# Revit family: Plumbing-Faucet-Sloan-Valve-SF-2250
name_source: partatom
category: Plumbing Fixtures
units: mm (PartAtom-declared; Revit-internal decimal feet)

## family parameters
Cut with Voids When Loaded = No
Host = Face
OmniClass Number = 23.45.55.14
OmniClass Title = Single Faucets
Part Type = Normal
Room Calculation Point = No
Round Connector Dimension = Use Diameter
Shared = No

## types (9) — shared parameters
Assembly Code = D2010
CW Connection = Yes
CWFU = 1.5
Cold Water Connection Diameter = 0"
Default Elevation = 0"
Depth = 6 5/8"
Edition number = 1
HW Connection = Yes
HWFU = 1.5
Height = 10"
Hot Water Connection Diameter = 0"
Keynote = 15410
Manufacturer = Sloan Valve
Product Material = Sloan Valve - Finish - Polished Chrome
Product data url = https://bimobject.com
URL = www.sloanvalve.com
Valve Pressure Drop = 0.00 psi
Vent Connection = No
Waste Connection = No
Width = 6 1/4"
z_Trim Plate Length = 6 1/4"
zero-valued in all types: WFU

## per-type parameters (varying)
| type | Description | Part Number | Water Flow |
| SF-2250-4-BAT-BDM-CP-0.35GPM-MLM-IR-FCT | 4" Trim Plate, Battery Power Supply, Below Deck Manual Mixing Valve, Polished Chrome Finish, 0.35 gpm, Multi-Laminar Spray, Infrared Sensor, Sloan® Battery-Powered Deck-Mounted Gooseneck Body Faucet. | 3362180 | 0 GPM |
| SF-2250-4-BAT-BDM-CP-1.0GPM-LAM-IR-FCT | 4" Trim Plate, Battery Power Supply, Below Deck Manual Mixing Valve, Polished Chrome Finish, 1.0 gpm, Laminar Spray, Infrared Sensor, Sloan® Battery-Powered Deck-Mounted Gooseneck Body Faucet. | 3362151 | 1 GPM |
| SF-2250-4-BAT-BDM-CP-1.5GPM-LAM-IR-FCT | 4" Trim Plate, Battery Power Supply, Below Deck Manual Mixing Valve, Polished Chrome Finish, 1.5 gpm, Laminar Spray, Infrared Sensor, Sloan® Battery-Powered Deck-Mounted Gooseneck Body Faucet. | 3362148 | 2 GPM |
| SF-2250-4-BAT-BDM-CP-2.2GPM-LAM-IR-FCT | 4" Trim Plate, Battery Power Supply, Below Deck Manual Mixing Valve, Polished Chrome Finish, 2.2 gpm, Laminar Spray, Infrared Sensor, Sloan® Battery-Powered Deck-Mounted Gooseneck Body Faucet. | 3362112 | 2 GPM |
| SF-2250-4-BAT-TEE-CP-0.35GPM-MLM-IR-FCT | 4" Trim Plate, Battery Power Supply, Back-Check Tee, Polished Chrome Finish, 0.35 gpm, Multi-Laminar Spray, Infrared Sensor, Sloan® Battery-Powered Deck-Mounted Gooseneck Body Faucet. | 3362173 | 0 GPM |
| SF-2250-4-BAT-TEE-CP-0.5GPM-MLM-IR-FCT | 4" Trim Plate, Battery Power Supply, Back-Check Tee, Polished Chrome Finish, 0.5 gpm, Multi-Laminar Spray, Infrared Sensor, Sloan® Battery-Powered Deck-Mounted Gooseneck Body Faucet. | 3362144 | 1 GPM |
| SF-2250-4-BAT-TEE-CP-1.0GPM-LAM-IR-FCT | 4" Trim Plate, Battery Power Supply, Back-Check Tee, Polished Chrome Finish, 1.0 gpm, Laminar Spray, Infrared Sensor, Sloan® Battery-Powered Deck-Mounted Gooseneck Body Faucet. | 3362150 | 1 GPM |
| SF-2250-4-BAT-TEE-CP-1.5GPM-LAM-IR-FCT | 4" Trim Plate, Battery Power Supply, Back-Check Tee, Polished Chrome Finish, 1.5 gpm, Laminar Spray, Infrared Sensor, Sloan® Battery-Powered Deck-Mounted Gooseneck Body Faucet. | 3362145 | 2 GPM |
| SF-2250-4-BAT-TEE-CP-2.2GPM-LAM-IR-FCT | 4" Trim Plate, Battery Power Supply, Back-Check Tee, Polished Chrome Finish, 2.2 gpm, Laminar Spray, Infrared Sensor, Sloan® Battery-Powered Deck-Mounted Gooseneck Body Faucet. | 3362104 | 2 GPM |

note: column(s) folded — value = type name in every type: Model

## geometry (parser evidence)
native form markers: Sweep x6
no freeform markers — native parametric forms only
